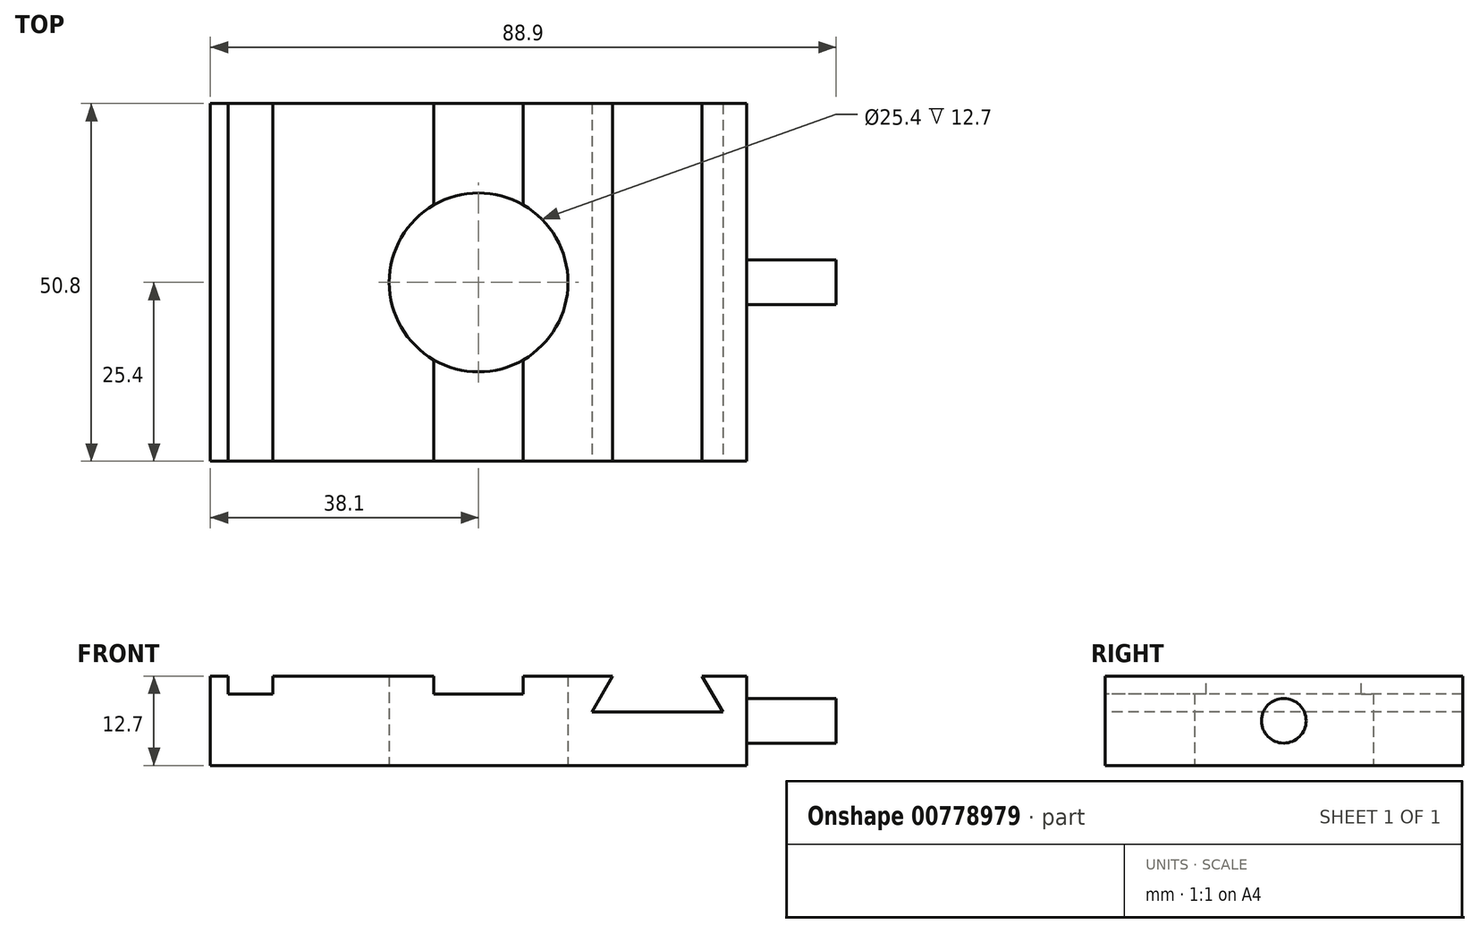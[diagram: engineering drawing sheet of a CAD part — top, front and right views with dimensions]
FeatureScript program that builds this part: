
annotation { "Feature Type Name" : "Feature", "Feature Type Description" : "" }
export const myFeature = defineFeature(function(context is Context, id is Id, definition is map)
    precondition{}
    {
        {
            var Q0;
            Q0=qCreatedBy(makeId("Top.planeOp"),FACE);
            var sketch = newSketch(context, id + "F0", { "sketchPlane" : qUnion([Q0])});
            skLineSegment(sketch, "E0.bottom", {"start": v(-38.1, 25.4) * mm, "end": v(38.1, 25.4) * mm});
            skLineSegment(sketch, "E0.top", {"start": v(-38.1, -25.4) * mm, "end": v(38.1, -25.4) * mm});
            skLineSegment(sketch, "E0.left", {"start": v(-38.1, 25.4) * mm, "end": v(-38.1, -25.4) * mm});
            skLineSegment(sketch, "E0.right", {"start": v(38.1, 25.4) * mm, "end": v(38.1, -25.4) * mm});
            skPoint(sketch, "E0.middle", {"position": v(0, 0) * mm});
            skCircle(sketch, "E1", {"center": v(0, 0) * mm, "radius": 12.7 * mm});
            skSolve(sketch);
        }
        {
            var Q0;
            Q0=makeQuery(id+"F0.imprint","IMPRINT",FACE,{"disambiguationData":[TD([[makeQuery(id+"F0.imprint","IMPRINT",EDGE,{"derivedFrom":sQuery(id+"F0.wireOp",EDGE,"E0.bottom")}),-1.0]])]});
            extrude(context, id + "F1", {"entities" : qUnion([Q0]), "depth" : 12.7 * mm, "offsetDistance" : 25.4 * mm});
        }
        {
            var Q0;
            Q0=makeQuery(id+"F1.opExtrude","CAP_FACE",FACE,{"disambiguationData":[OSD([sQuery(id+"F0.wireOp",EDGE,"E0.bottom"),sQuery(id+"F0.wireOp",EDGE,"E0.top"),sQuery(id+"F0.wireOp",EDGE,"E0.left"),sQuery(id+"F0.wireOp",EDGE,"E0.right"),sQuery(id+"F0.wireOp",EDGE,"E1")])],"isStart":false});
            var sketch = newSketch(context, id + "F2", { "sketchPlane" : qUnion([Q0])});
            skLineSegment(sketch, "E2.bottom", {"start": v(-35.56, 25.4) * mm, "end": v(-29.2, 25.4) * mm});
            skLineSegment(sketch, "E2.top", {"start": v(-35.56, -25.4) * mm, "end": v(-29.2, -25.4) * mm});
            skLineSegment(sketch, "E2.left", {"start": v(-35.56, 25.4) * mm, "end": v(-35.56, -25.4) * mm});
            skLineSegment(sketch, "E2.right", {"start": v(-29.2, 25.4) * mm, "end": v(-29.2, -25.4) * mm});
            skLineSegment(sketch, "E3", {"start": v(-6.35, 25.4) * mm, "end": v(-6.35, -25.4) * mm});
            skLineSegment(sketch, "E4", {"start": v(-6.35, -25.4) * mm, "end": v(6.35, -25.4) * mm});
            skLineSegment(sketch, "E5", {"start": v(6.35, -25.4) * mm, "end": v(6.35, 25.4) * mm});
            skLineSegment(sketch, "E6", {"start": v(6.35, 25.4) * mm, "end": v(-6.35, 25.4) * mm});
            skPoint(sketch, "E7", {"position": v(0, 0) * mm});
            skLineSegment(sketch, "E8", {"start": v(0, 25.4) * mm, "end": v(0, -25.4) * mm, "construction": true});
            skSolve(sketch);
        }
        {
            var Q0;
            Q0=makeQuery(id+"F2.imprint","IMPRINT",FACE,{"disambiguationData":[TD([[makeQuery(id+"F2.imprint","IMPRINT",EDGE,{"derivedFrom":sQuery(id+"F2.wireOp",EDGE,"E2.bottom")}),-1.0]])]});
            var Q1;
            {var subQ0=sQuery(id+"F2.wireOp",EDGE,"E6");Q1=makeQuery(id+"F2.imprint","IMPRINT",FACE,{"disambiguationData":[TD([[makeQuery(id+"F2.imprint","IMPRINT",EDGE,{"derivedFrom":subQ0}),-1.0]])]});}
            var Q2;
            {var subQ0=sQuery(id+"F2.wireOp",EDGE,"E4");Q2=makeQuery(id+"F2.imprint","IMPRINT",FACE,{"disambiguationData":[TD([[makeQuery(id+"F2.imprint","IMPRINT",EDGE,{"derivedFrom":subQ0}),1.0]])]});}
            extrude(context, id + "F3", {"entities" : qUnion([Q0, Q1, Q2]), "operationType" : NewBodyOperationType.REMOVE, "oppositeDirection" : true, "depth" : 2.54 * mm, "offsetDistance" : 25.4 * mm});
        }
        {
            var Q0;
            Q0=makeQuery(id+"F1.opExtrude","SWEPT_FACE",FACE,{"disambiguationData":[OSD([sQuery(id+"F0.wireOp",EDGE,"E0.top")])]});
            var sketch = newSketch(context, id + "F4", { "sketchPlane" : qUnion([Q0])});
            skLineSegment(sketch, "E9", {"start": v(19.05, 12.7) * mm, "end": v(16.12, 7.62) * mm});
            skLineSegment(sketch, "E10", {"start": v(16.12, 7.62) * mm, "end": v(34.68, 7.62) * mm});
            skLineSegment(sketch, "E11", {"start": v(34.68, 7.62) * mm, "end": v(31.75, 12.7) * mm});
            skLineSegment(sketch, "E12", {"start": v(19.05, 12.7) * mm, "end": v(31.75, 12.7) * mm});
            skLineSegment(sketch, "E13", {"start": v(25.4, 7.62) * mm, "end": v(25.4, 12.7) * mm, "construction": true});
            skSolve(sketch);
        }
        {
            var Q0;
            Q0 = qSketchRegion(id + "F4", true);
            extrude(context, id + "F5", {"entities" : qUnion([Q0]), "operationType" : NewBodyOperationType.REMOVE, "endBound" : BoundingType.THROUGH_ALL, "oppositeDirection" : true, "depth" : 12.7 * mm, "offsetDistance" : 25.4 * mm});
        }
        {
            var Q0;
            Q0=makeQuery(id+"F1.opExtrude","SWEPT_FACE",FACE,{"disambiguationData":[OSD([sQuery(id+"F0.wireOp",EDGE,"E0.right")])]});
            var sketch = newSketch(context, id + "F6", { "sketchPlane" : qUnion([Q0])});
            skLineSegment(sketch, "E14", {"start": v(0, 12.7) * mm, "end": v(0, 0) * mm, "construction": true});
            skLineSegment(sketch, "E15", {"start": v(-25.4, 6.35) * mm, "end": v(25.4, 6.35) * mm, "construction": true});
            skCircle(sketch, "E16", {"center": v(0, 6.35) * mm, "radius": 3.18 * mm});
            skSolve(sketch);
        }
        {
            var Q0;
            Q0 = qSketchRegion(id + "F6", true);
            var Q1;
            Q1=sQuery(id+"F6.wireOp",EDGE,"E16");
            extrude(context, id + "F7", {"entities" : qUnion([Q0]), "operationType" : NewBodyOperationType.ADD, "surfaceOperationType" : NewSurfaceOperationType.ADD, "surfaceEntities" : qUnion([Q1]), "depth" : 12.7 * mm, "offsetDistance" : 25.4 * mm});
        }
    });
